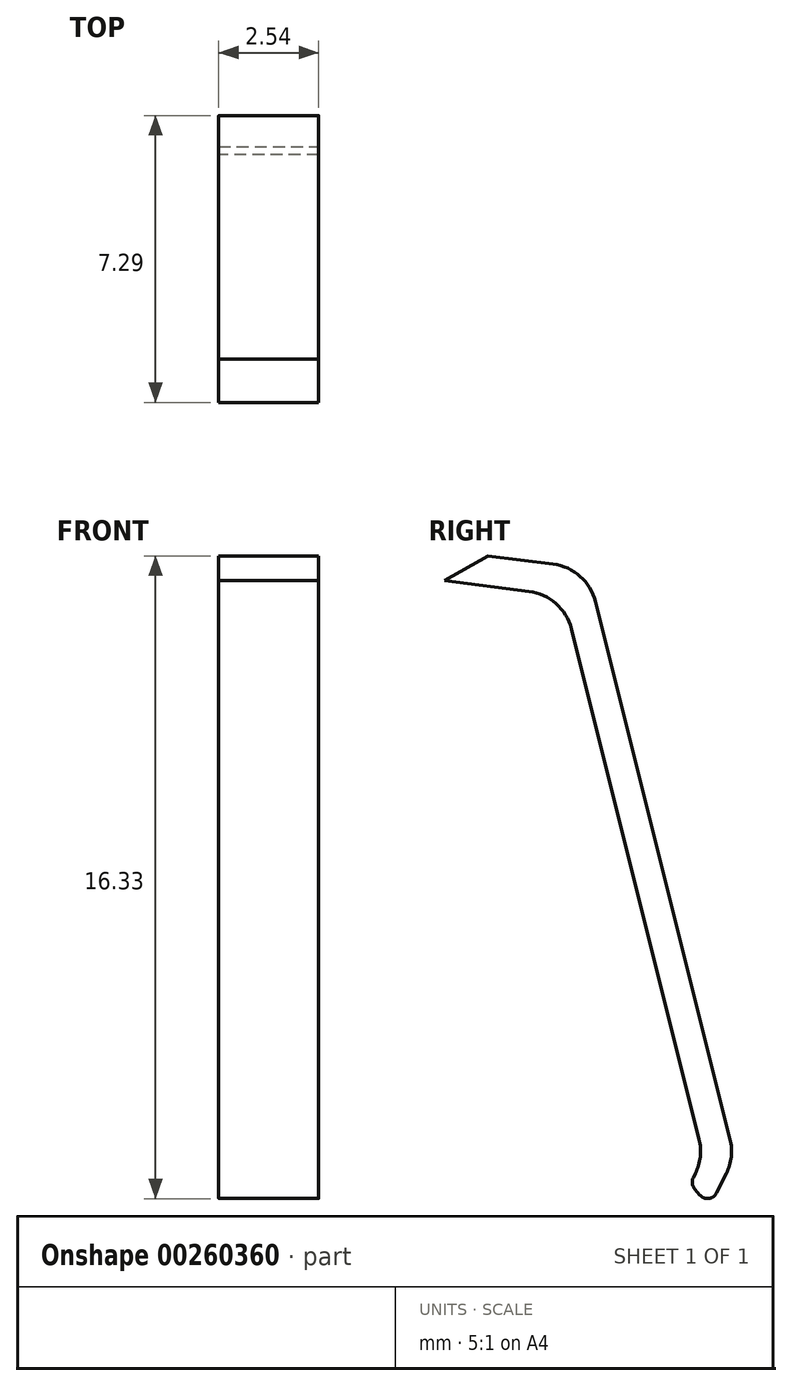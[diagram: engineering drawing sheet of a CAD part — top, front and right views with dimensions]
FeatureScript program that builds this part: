
annotation { "Feature Type Name" : "Feature", "Feature Type Description" : "" }
export const myFeature = defineFeature(function(context is Context, id is Id, definition is map)
    precondition{}
    {
        {
            var Q0;
            Q0=qCreatedBy(makeId("Right.planeOp"),FACE);
            var sketch = newSketch(context, id + "F0", { "sketchPlane" : qUnion([Q0])});
            skLineSegment(sketch, "E0", {"start": v(-30.36, 12.62) * mm, "end": v(-29.26, 13.25) * mm});
            skLineSegment(sketch, "E1", {"start": v(-29.26, 13.25) * mm, "end": v(-26.74, 12.93) * mm});
            skPoint(sketch, "E1.endSnap0", {"position": v(-29.8, 12.93) * mm});
            skLineSegment(sketch, "E2", {"start": v(-26.74, 12.93) * mm, "end": v(-23, -2.02) * mm});
            skLineSegment(sketch, "E3", {"start": v(-23, -2.02) * mm, "end": v(-23.62, -3.28) * mm});
            skLineSegment(sketch, "E4", {"start": v(-30.36, 12.62) * mm, "end": v(-27.35, 12.24) * mm});
            skLineSegment(sketch, "E5", {"start": v(-27.35, 12.24) * mm, "end": v(-23.78, -2.02) * mm});
            skLineSegment(sketch, "E6", {"start": v(-23.78, -2.02) * mm, "end": v(-24.12, -2.7) * mm});
            skLineSegment(sketch, "E7", {"start": v(-24.12, -2.7) * mm, "end": v(-23.62, -3.28) * mm});
            skSolve(sketch);
        }
        {
            var Q0;
            Q0=makeQuery(id+"F0.imprint","IMPRINT",FACE,{"disambiguationData":[TD([[makeQuery(id+"F0.imprint","IMPRINT",EDGE,{"derivedFrom":sQuery(id+"F0.wireOp",EDGE,"E0")}),-1.0]])]});
            extrude(context, id + "F1", {"entities" : qUnion([Q0]), "depth" : 2.54 * mm});
        }
        {
            var Q0;
            Q0=makeQuery(id+"F1.opExtrude","SWEPT_EDGE",EDGE,{"disambiguationData":[OSD([sQuery(id+"F0.wireOp",EDGE,"E2"),sQuery(id+"F0.wireOp",EDGE,"E3")])]});
            fillet(context, id + "F2", {"entities" : qUnion([Q0]), "radius" : 1.27 * mm, "tangentPropagation" : true, "allowEdgeOverflow" : false});
        }
        {
            var Q0;
            Q0=makeQuery(id+"F1.opExtrude","SWEPT_EDGE",EDGE,{"disambiguationData":[OSD([sQuery(id+"F0.wireOp",EDGE,"E3"),sQuery(id+"F0.wireOp",EDGE,"E7")])]});
            fillet(context, id + "F3", {"entities" : qUnion([Q0]), "radius" : 0.25 * mm, "tangentPropagation" : true, "allowEdgeOverflow" : false});
        }
        {
            var Q0;
            Q0=makeQuery(id+"F1.opExtrude","SWEPT_EDGE",EDGE,{"disambiguationData":[OSD([sQuery(id+"F0.wireOp",EDGE,"E5"),sQuery(id+"F0.wireOp",EDGE,"E6")])]});
            fillet(context, id + "F4", {"entities" : qUnion([Q0]), "radius" : 1.27 * mm, "tangentPropagation" : true, "allowEdgeOverflow" : false});
        }
        {
            var Q0;
            Q0=makeQuery(id+"F1.opExtrude","SWEPT_EDGE",EDGE,{"disambiguationData":[OSD([sQuery(id+"F0.wireOp",EDGE,"E6"),sQuery(id+"F0.wireOp",EDGE,"E7")])]});
            fillet(context, id + "F5", {"entities" : qUnion([Q0]), "radius" : 0.25 * mm, "tangentPropagation" : true, "allowEdgeOverflow" : false});
        }
        {
            var Q0;
            Q0=makeQuery(id+"F1.opExtrude","SWEPT_EDGE",EDGE,{"disambiguationData":[OSD([sQuery(id+"F0.wireOp",EDGE,"E1"),sQuery(id+"F0.wireOp",EDGE,"E2")])]});
            fillet(context, id + "F6", {"entities" : qUnion([Q0]), "radius" : 1.27 * mm, "tangentPropagation" : true, "allowEdgeOverflow" : false});
        }
        {
            var Q0;
            Q0=makeQuery(id+"F1.opExtrude","SWEPT_EDGE",EDGE,{"disambiguationData":[OSD([sQuery(id+"F0.wireOp",EDGE,"E4"),sQuery(id+"F0.wireOp",EDGE,"E5")])]});
            fillet(context, id + "F7", {"entities" : qUnion([Q0]), "radius" : 1.27 * mm, "tangentPropagation" : true, "allowEdgeOverflow" : false});
        }
    });
